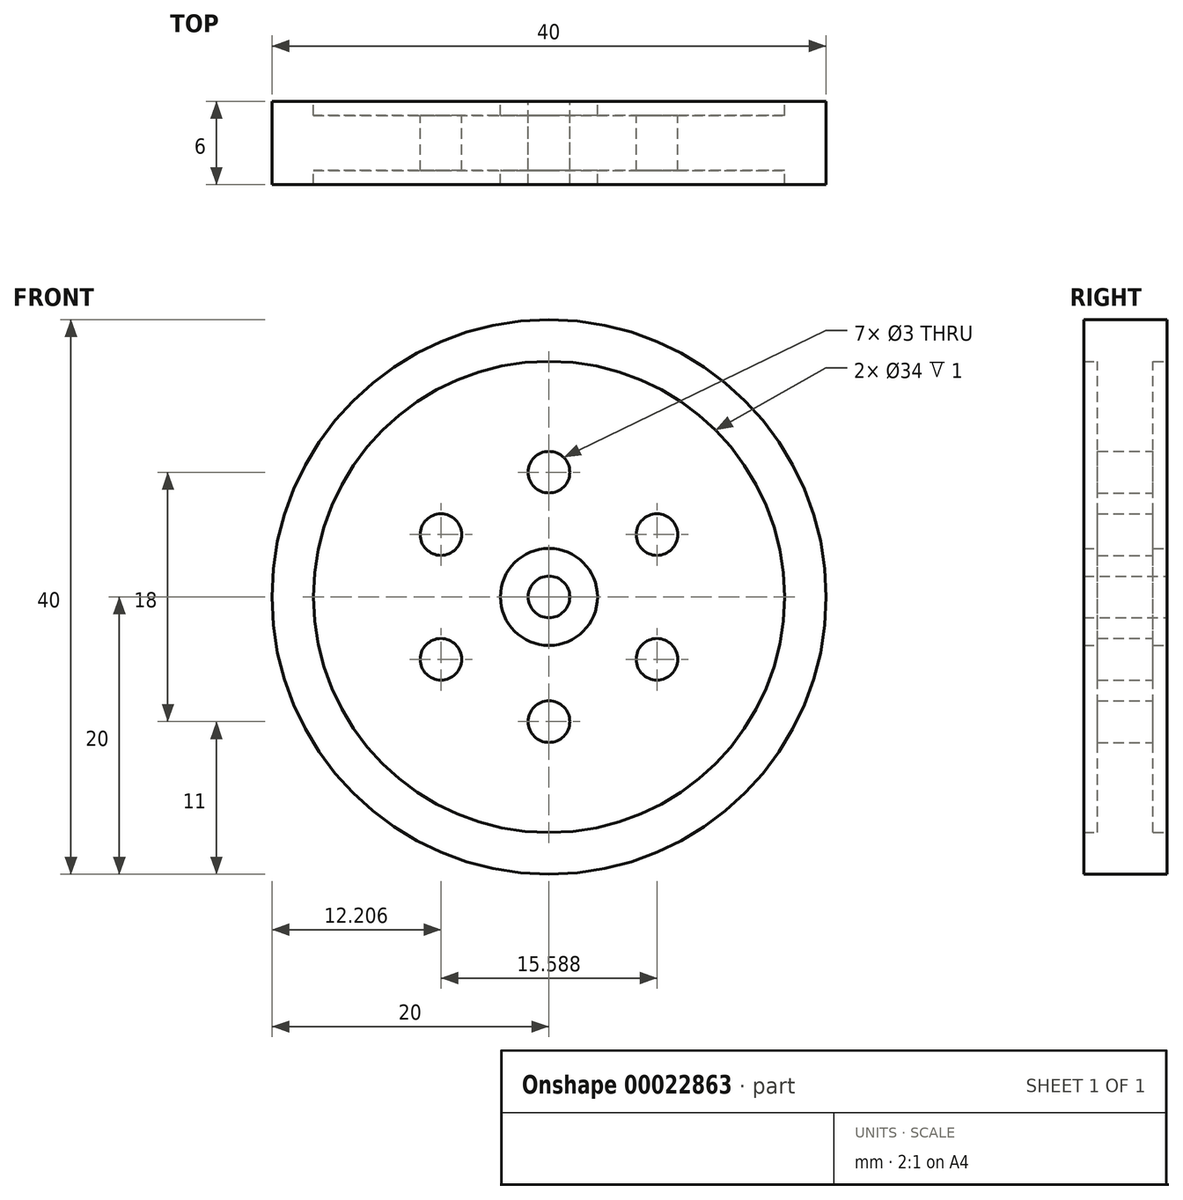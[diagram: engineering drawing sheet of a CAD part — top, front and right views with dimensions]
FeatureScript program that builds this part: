
annotation { "Feature Type Name" : "Feature", "Feature Type Description" : "" }
export const myFeature = defineFeature(function(context is Context, id is Id, definition is map)
    precondition{}
    {
        {
            var Q0;
            Q0=qCreatedBy(makeId("Front.planeOp"),FACE);
            var sketch = newSketch(context, id + "F0", { "sketchPlane" : qUnion([Q0])});
            skCircle(sketch, "E0", {"center": v(0, 0) * mm, "radius": 17 * mm});
            skCircle(sketch, "E1", {"center": v(0, 0) * mm, "radius": 1.5 * mm});
            skCircle(sketch, "E2", {"center": v(0, 9) * mm, "radius": 1.5 * mm});
            skCircle(sketch, "E3", {"center": v(0, 0) * mm, "radius": 20 * mm});
            skCircle(sketch, "E4", {"center": v(0, 0) * mm, "radius": 3.5 * mm});
            skCircle(sketch, "E5.1.0", {"center": v(-7.8, 4.5) * mm, "radius": 1.5 * mm});
            skCircle(sketch, "E5.2.0", {"center": v(-7.8, -4.5) * mm, "radius": 1.5 * mm});
            skCircle(sketch, "E5.3.0", {"center": v(0, -9) * mm, "radius": 1.5 * mm});
            skCircle(sketch, "E6.1.4.0", {"center": v(7.8, -4.5) * mm, "radius": 1.5 * mm});
            skCircle(sketch, "E6.1.5.0", {"center": v(7.8, 4.5) * mm, "radius": 1.5 * mm});
            skSolve(sketch);
        }
        {
            var Q0;
            Q0=makeQuery(id+"F0.imprint","IMPRINT",FACE,{"disambiguationData":[TD([[makeQuery(id+"F0.imprint","IMPRINT",EDGE,{"derivedFrom":sQuery(id+"F0.wireOp",EDGE,"E0")}),-1.0]])]});
            extrude(context, id + "F1", {"entities" : qUnion([Q0]), "endBound" : BoundingType.SYMMETRIC, "depth" : 6 * mm});
        }
        {
            var Q0;
            Q0=makeQuery(id+"F0.imprint","IMPRINT",FACE,{"disambiguationData":[TD([[makeQuery(id+"F0.imprint","IMPRINT",EDGE,{"derivedFrom":sQuery(id+"F0.wireOp",EDGE,"E0")}),1.0]])]});
            extrude(context, id + "F2", {"entities" : qUnion([Q0]), "operationType" : NewBodyOperationType.ADD, "endBound" : BoundingType.SYMMETRIC, "depth" : 4 * mm});
        }
        {
            var Q0;
            Q0=makeQuery(id+"F0.imprint","IMPRINT",FACE,{"disambiguationData":[TD([[makeQuery(id+"F0.imprint","IMPRINT",EDGE,{"derivedFrom":sQuery(id+"F0.wireOp",EDGE,"E1")}),-1.0]])]});
            extrude(context, id + "F3", {"entities" : qUnion([Q0]), "operationType" : NewBodyOperationType.ADD, "endBound" : BoundingType.SYMMETRIC, "depth" : 6 * mm});
        }
    });
